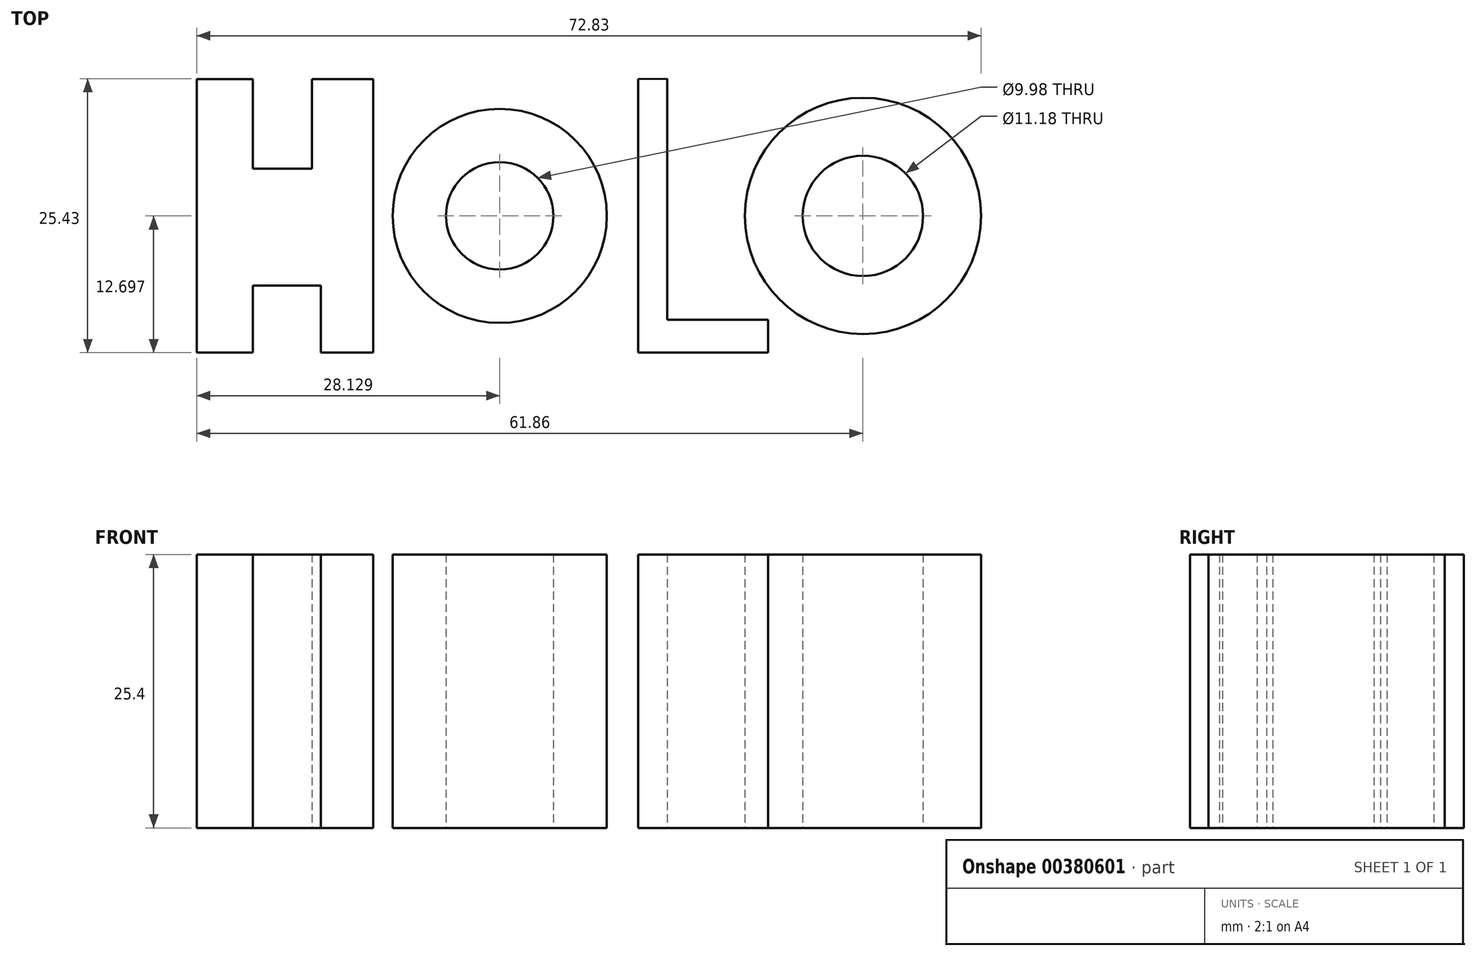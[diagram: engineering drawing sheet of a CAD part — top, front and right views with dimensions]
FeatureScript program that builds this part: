
annotation { "Feature Type Name" : "Feature", "Feature Type Description" : "" }
export const myFeature = defineFeature(function(context is Context, id is Id, definition is map)
    precondition{}
    {
        {
            var Q0;
            Q0=qCreatedBy(makeId("Top.planeOp"),FACE);
            var sketch = newSketch(context, id + "F0", { "sketchPlane" : qUnion([Q0])});
            skCircle(sketch, "E0", {"center": v(-33.73, 9.66) * mm, "radius": 9.94 * mm});
            skLineSegment(sketch, "E1", {"start": v(-20.88, 22.36) * mm, "end": v(-20.88, -3.04) * mm});
            skLineSegment(sketch, "E2", {"start": v(-20.88, -3.04) * mm, "end": v(-8.8, -3.04) * mm});
            skCircle(sketch, "E3", {"center": v(0, 9.66) * mm, "radius": 10.97 * mm});
            skCircle(sketch, "E4", {"center": v(-33.73, 9.66) * mm, "radius": 4.99 * mm});
            skCircle(sketch, "E5", {"center": v(0, 9.66) * mm, "radius": 5.59 * mm});
            skLineSegment(sketch, "E6", {"start": v(-8.8, -3.04) * mm, "end": v(-8.8, 0) * mm});
            skLineSegment(sketch, "E7", {"start": v(-8.8, 0) * mm, "end": v(-18.17, 0) * mm});
            skLineSegment(sketch, "E8", {"start": v(-18.17, 0) * mm, "end": v(-18.17, 22.4) * mm});
            skLineSegment(sketch, "E9", {"start": v(-18.17, 22.4) * mm, "end": v(-20.88, 22.36) * mm});
            skLineSegment(sketch, "E10", {"start": v(-45.48, 22.36) * mm, "end": v(-45.48, -3.04) * mm});
            skLineSegment(sketch, "E11", {"start": v(-45.48, -3.04) * mm, "end": v(-50.34, -3.04) * mm});
            skLineSegment(sketch, "E12", {"start": v(-50.34, -3.04) * mm, "end": v(-50.34, 3.18) * mm});
            skLineSegment(sketch, "E13", {"start": v(-50.34, 3.18) * mm, "end": v(-56.67, 3.18) * mm});
            skLineSegment(sketch, "E14", {"start": v(-56.67, 3.18) * mm, "end": v(-56.67, -3.04) * mm});
            skPoint(sketch, "E14.endSnap0", {"position": v(-47.9, -3.04) * mm});
            skLineSegment(sketch, "E15", {"start": v(-56.67, -3.04) * mm, "end": v(-61.86, -3.04) * mm});
            skLineSegment(sketch, "E16", {"start": v(-61.86, -3.04) * mm, "end": v(-61.86, 22.36) * mm});
            skLineSegment(sketch, "E17", {"start": v(-61.86, 22.36) * mm, "end": v(-56.67, 22.36) * mm});
            skLineSegment(sketch, "E18", {"start": v(-56.67, 22.36) * mm, "end": v(-56.67, 14.05) * mm});
            skLineSegment(sketch, "E19", {"start": v(-56.67, 14.05) * mm, "end": v(-51.15, 14.05) * mm});
            skLineSegment(sketch, "E20", {"start": v(-51.15, 14.05) * mm, "end": v(-51.15, 22.36) * mm});
            skLineSegment(sketch, "E21", {"start": v(-51.15, 22.36) * mm, "end": v(-45.48, 22.36) * mm});
            skSolve(sketch);
        }
        {
            var Q0;
            Q0=makeQuery(id+"F0.imprint","IMPRINT",FACE,{"disambiguationData":[TD([[makeQuery(id+"F0.imprint","IMPRINT",EDGE,{"derivedFrom":sQuery(id+"F0.wireOp",EDGE,"E0")}),1.0]])]});
            var Q1;
            Q1=makeQuery(id+"F0.imprint","IMPRINT",FACE,{"disambiguationData":[TD([[makeQuery(id+"F0.imprint","IMPRINT",EDGE,{"derivedFrom":sQuery(id+"F0.wireOp",EDGE,"E10")}),-1.0]])]});
            var Q2;
            Q2=makeQuery(id+"F0.imprint","IMPRINT",FACE,{"disambiguationData":[TD([[makeQuery(id+"F0.imprint","IMPRINT",EDGE,{"derivedFrom":sQuery(id+"F0.wireOp",EDGE,"E1")}),1.0]])]});
            var Q3;
            Q3=makeQuery(id+"F0.imprint","IMPRINT",FACE,{"disambiguationData":[TD([[makeQuery(id+"F0.imprint","IMPRINT",EDGE,{"derivedFrom":sQuery(id+"F0.wireOp",EDGE,"E3")}),1.0]])]});
            extrude(context, id + "F1", {"entities" : qUnion([Q0, Q1, Q2, Q3]), "depth" : 25.4 * mm});
        }
    });
